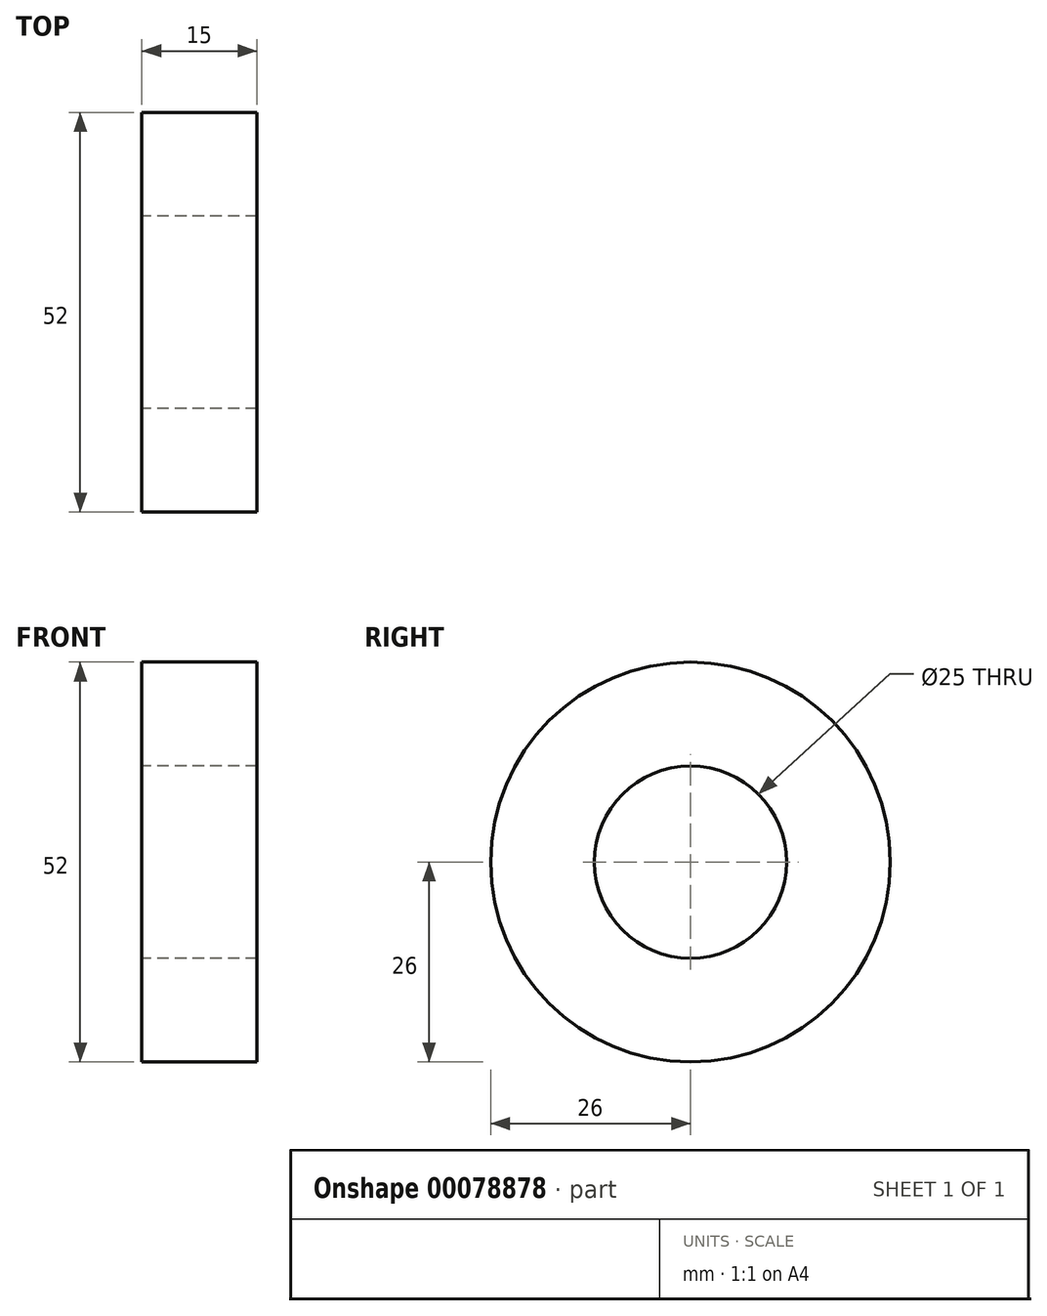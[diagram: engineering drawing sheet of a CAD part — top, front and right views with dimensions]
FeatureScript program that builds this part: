
annotation { "Feature Type Name" : "Feature", "Feature Type Description" : "" }
export const myFeature = defineFeature(function(context is Context, id is Id, definition is map)
    precondition{}
    {
        {
            var Q0;
            Q0=qCreatedBy(makeId("Front.planeOp"),FACE);
            var sketch = newSketch(context, id + "F0", { "sketchPlane" : qUnion([Q0])});
            skLineSegment(sketch, "E0.bottom", {"start": v(-8.45, 26) * mm, "end": v(6.55, 26) * mm});
            skLineSegment(sketch, "E0.top", {"start": v(-8.45, 12.5) * mm, "end": v(6.55, 12.5) * mm});
            skLineSegment(sketch, "E0.left", {"start": v(-8.45, 26) * mm, "end": v(-8.45, 12.5) * mm});
            skLineSegment(sketch, "E0.right", {"start": v(6.55, 26) * mm, "end": v(6.55, 12.5) * mm});
            skLineSegment(sketch, "E1", {"start": v(-59.12, 0) * mm, "end": v(0, 0) * mm, "construction": true});
            skSolve(sketch);
        }
        {
            var Q0;
            Q0=makeQuery(id+"F0.imprint","IMPRINT",FACE,{"disambiguationData":[TD([[makeQuery(id+"F0.imprint","IMPRINT",EDGE,{"derivedFrom":sQuery(id+"F0.wireOp",EDGE,"E0.bottom")}),-1.0]])]});
            var Q1;
            Q1=sQuery(id+"F0.wireOp",EDGE,"E1");
            revolve(context, id + "F1", {"entities" : qUnion([Q0]), "axis" : qUnion([Q1]), "revolveType" : RevolveType.FULL});
        }
    });
